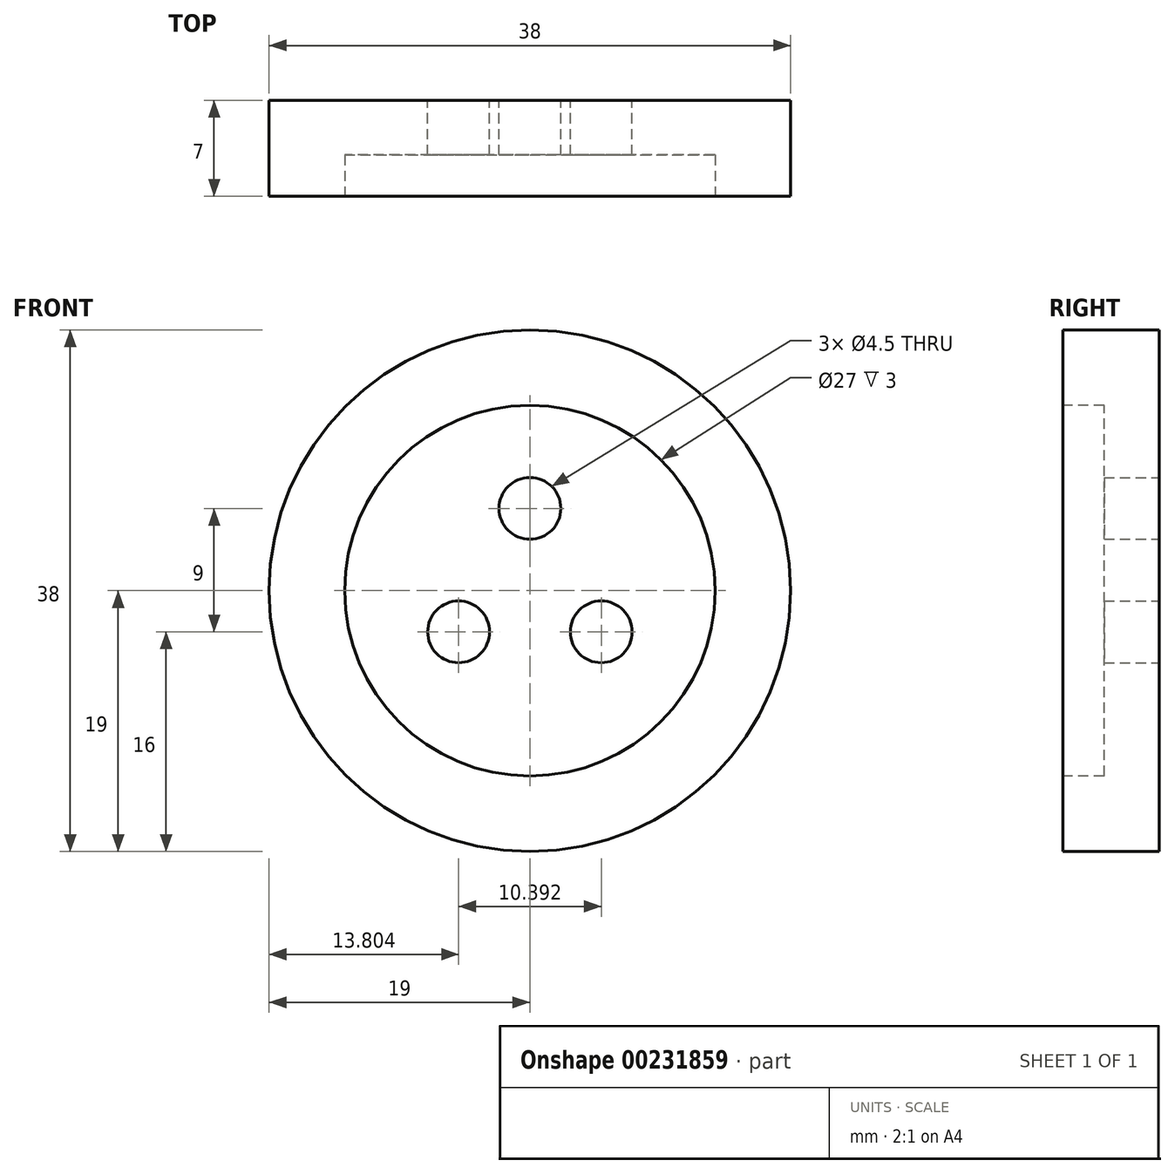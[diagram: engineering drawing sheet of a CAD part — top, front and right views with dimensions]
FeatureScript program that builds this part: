
annotation { "Feature Type Name" : "Feature", "Feature Type Description" : "" }
export const myFeature = defineFeature(function(context is Context, id is Id, definition is map)
    precondition{}
    {
        {
            var Q0;
            Q0=qCreatedBy(makeId("Right.planeOp"),FACE);
            var sketch = newSketch(context, id + "F0", { "sketchPlane" : qUnion([Q0])});
            skLineSegment(sketch, "E0.bottom", {"start": v(0, 19) * mm, "end": v(7, 19) * mm});
            skLineSegment(sketch, "E0.left", {"start": v(0, 19) * mm, "end": v(0, 13.5) * mm});
            skLineSegment(sketch, "E0.right", {"start": v(7, 19) * mm, "end": v(7, 0) * mm});
            skPoint(sketch, "E0.middle", {"position": v(0, 0) * mm});
            skLineSegment(sketch, "E1", {"start": v(3, 0) * mm, "end": v(7, 0) * mm});
            skLineSegment(sketch, "E2", {"start": v(0, 13.5) * mm, "end": v(3, 13.5) * mm});
            skLineSegment(sketch, "E3", {"start": v(3, 13.5) * mm, "end": v(3, 0) * mm});
            skSolve(sketch);
        }
        {
            var Q0;
            Q0=makeQuery(id+"F0.imprint","IMPRINT",FACE,{"disambiguationData":[TD([[makeQuery(id+"F0.imprint","IMPRINT",EDGE,{"derivedFrom":sQuery(id+"F0.wireOp",EDGE,"E0.bottom")}),-1.0]])]});
            var Q1;
            Q1=sQuery(id+"F0.wireOp",EDGE,"E1");
            revolve(context, id + "F1", {"entities" : qUnion([Q0]), "axis" : qUnion([Q1]), "revolveType" : RevolveType.FULL});
        }
        {
            var Q0;
            Q0=makeQuery(id+"F1.opRevolve","SWEPT_FACE",FACE,{"disambiguationData":[OSD([sQuery(id+"F0.wireOp",EDGE,"E0.right")])]});
            var sketch = newSketch(context, id + "F2", { "sketchPlane" : qUnion([Q0])});
            skCircle(sketch, "E4", {"center": v(0, 0) * mm, "radius": 6 * mm});
            skLineSegment(sketch, "E5", {"start": v(0, 6) * mm, "end": v(0, 0) * mm});
            skLineSegment(sketch, "E6", {"start": v(-5.2, -3) * mm, "end": v(0, 0) * mm});
            skLineSegment(sketch, "E7", {"start": v(5.2, -3) * mm, "end": v(0, 0) * mm});
            skPoint(sketch, "E8", {"position": v(0, 6) * mm});
            skPoint(sketch, "E9", {"position": v(-5.2, -3) * mm});
            skPoint(sketch, "E10", {"position": v(5.2, -3) * mm});
            skSolve(sketch);
        }
        {
            var Q0;
            Q0=sQuery(id+"F2.wireOp",VERTEX,"E8");
            var Q1;
            Q1=sQuery(id+"F2.wireOp",VERTEX,"E9");
            var Q2;
            Q2=sQuery(id+"F2.wireOp",VERTEX,"E10");
            var Q3;
            Q3=makeQuery(id+"F1.opRevolve","SWEPT_BODY",BODY,{"disambiguationData":[OSD([sQuery(id+"F0.wireOp",EDGE,"E0.bottom"),sQuery(id+"F0.wireOp",EDGE,"E0.left"),sQuery(id+"F0.wireOp",EDGE,"E0.right"),sQuery(id+"F0.wireOp",EDGE,"E1"),sQuery(id+"F0.wireOp",EDGE,"E2"),sQuery(id+"F0.wireOp",EDGE,"E3")])]});
            hole(context, id + "F3", {"style" : HoleStyle.SIMPLE, "endStyle" : HoleEndStyle.THROUGH, "holeDiameter" : 4.5 * mm, "startFromSketch" : true, "locations" : qUnion([Q0, Q1, Q2]), "scope" : qUnion([Q3]), "isTappedThrough" : true});
        }
    });
